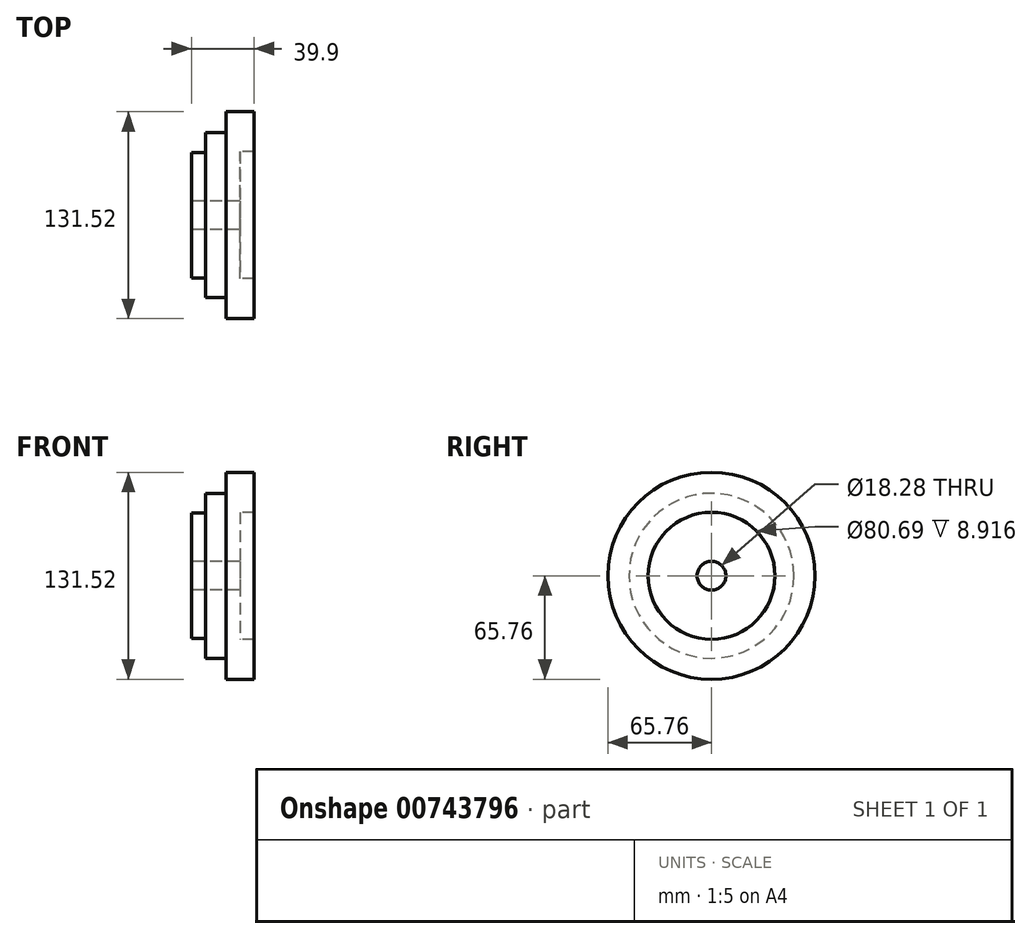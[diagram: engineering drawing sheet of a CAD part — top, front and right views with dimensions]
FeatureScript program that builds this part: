
annotation { "Feature Type Name" : "Feature", "Feature Type Description" : "" }
export const myFeature = defineFeature(function(context is Context, id is Id, definition is map)
    precondition{}
    {
        {
            var Q0;
            Q0=qCreatedBy(makeId("Front.planeOp"),FACE);
            var sketch = newSketch(context, id + "F0", { "sketchPlane" : qUnion([Q0])});
            skLineSegment(sketch, "E0", {"start": v(0, 0) * mm, "end": v(39.9, 0) * mm});
            skLineSegment(sketch, "E1", {"start": v(0, 0) * mm, "end": v(0, 39.9) * mm});
            skLineSegment(sketch, "E2", {"start": v(0, 39.9) * mm, "end": v(9.14, 39.9) * mm});
            skLineSegment(sketch, "E3", {"start": v(9.14, 39.9) * mm, "end": v(9.14, 52.38) * mm});
            skLineSegment(sketch, "E4", {"start": v(9.14, 52.38) * mm, "end": v(22.07, 52.38) * mm});
            skLineSegment(sketch, "E5", {"start": v(22.07, 52.38) * mm, "end": v(22.07, 65.76) * mm});
            skLineSegment(sketch, "E6", {"start": v(22.07, 65.76) * mm, "end": v(39.9, 65.76) * mm});
            skLineSegment(sketch, "E7", {"start": v(39.9, 65.76) * mm, "end": v(39.9, 0) * mm});
            skLineSegment(sketch, "E8", {"start": v(0, 9.14) * mm, "end": v(39.9, 9.14) * mm});
            skLineSegment(sketch, "E9", {"start": v(39.9, 40.35) * mm, "end": v(30.98, 40.35) * mm});
            skLineSegment(sketch, "E10", {"start": v(30.98, 40.35) * mm, "end": v(30.98, 9.14) * mm});
            skSolve(sketch);
        }
        {
            var Q0;
            {var subQ0=sQuery(id+"F0.wireOp",EDGE,"E2");Q0=makeQuery(id+"F0.imprint","IMPRINT",FACE,{"disambiguationData":[TD([[makeQuery(id+"F0.imprint","IMPRINT",EDGE,{"derivedFrom":subQ0}),-1.0]])]});}
            var Q1;
            Q1=sQuery(id+"F0.wireOp",EDGE,"E0");
            revolve(context, id + "F1", {"surfaceOperationType" : NewSurfaceOperationType.NEW, "entities" : qUnion([Q0]), "axis" : qUnion([Q1]), "revolveType" : RevolveType.FULL});
        }
    });
